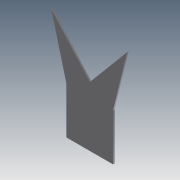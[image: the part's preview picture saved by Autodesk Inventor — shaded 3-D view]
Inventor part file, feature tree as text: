
AUTODESK INVENTOR PART (.ipt)
format: ipt  version: 2011 (Build 150239000, 239)  size: 86,016 bytes
history: native  units: in
note: dims shown in document units (in); Inventor stores cm internally (conversion verified against a paired STEP export)
features: extrude x1, sketch x1
ambient origin geometry x8: Origin, YZ Plane, XZ Plane, XY Plane, X Axis, Y Axis, Z Axis, Center Point
bodies: Solid1 (feature_tree)
feature tree (2):
  extrude  "Extrusion1"  Depth=4.0in
  sketch  "Sketch1"  dims[d0=4.0in d1=4.0in d2=0.2749in d3=0.962in d4=2.0in d5=2.0in d6=5.0in d7=5.0in d8=0.125in d9=0.0in]
